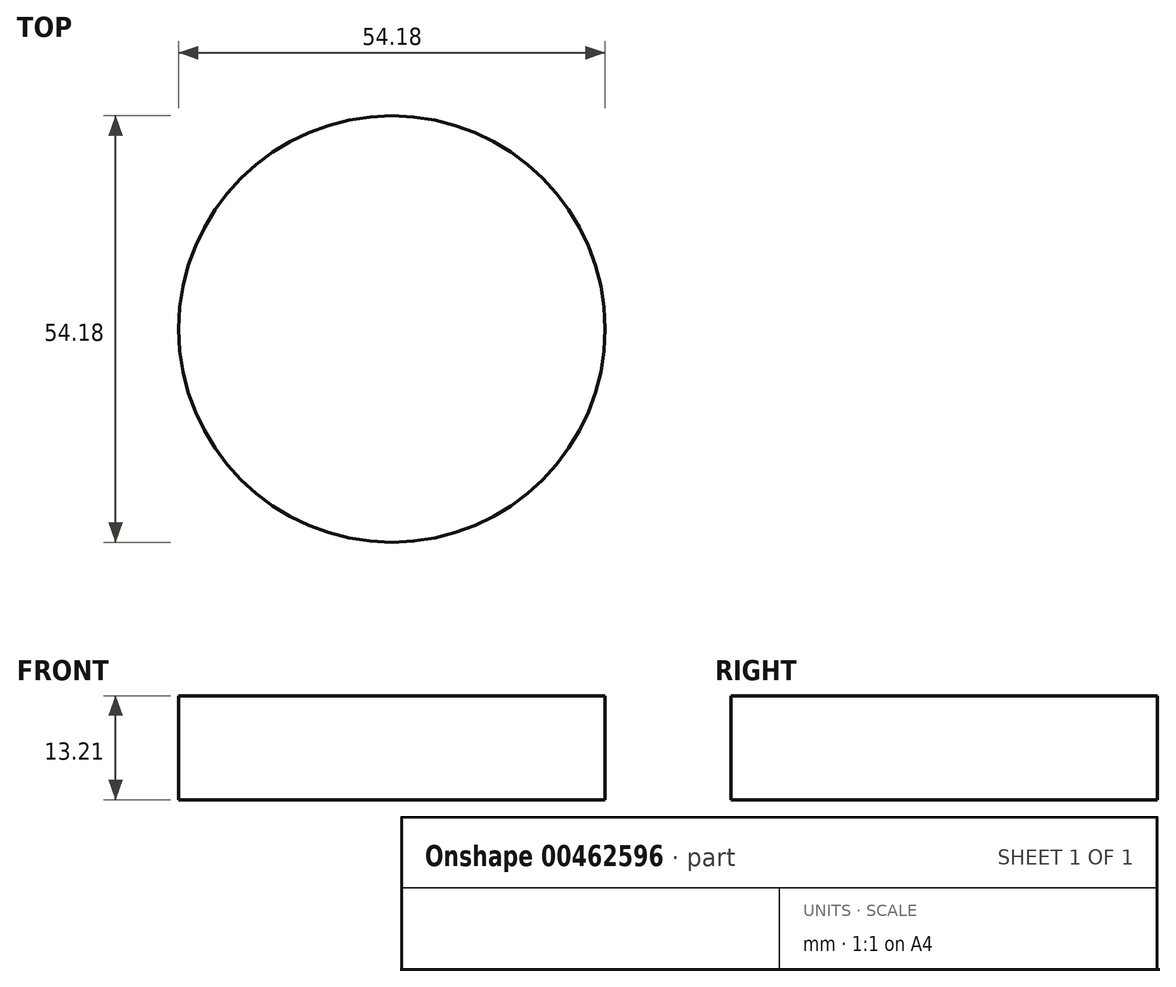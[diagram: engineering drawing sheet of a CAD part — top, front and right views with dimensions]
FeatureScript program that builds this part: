
annotation { "Feature Type Name" : "Feature", "Feature Type Description" : "" }
export const myFeature = defineFeature(function(context is Context, id is Id, definition is map)
    precondition{}
    {
        {
            var Q0;
            Q0=qCreatedBy(makeId("Top.planeOp"),FACE);
            var sketch = newSketch(context, id + "F0", { "sketchPlane" : qUnion([Q0])});
            skCircle(sketch, "E0", {"center": v(0, 0) * mm, "radius": 27.09 * mm});
            skSolve(sketch);
        }
        {
            var Q0;
            Q0 = qSketchRegion(id + "F0", true);
            extrude(context, id + "F1", {"entities" : qUnion([Q0]), "depth" : 13.2 * mm});
        }
    });
